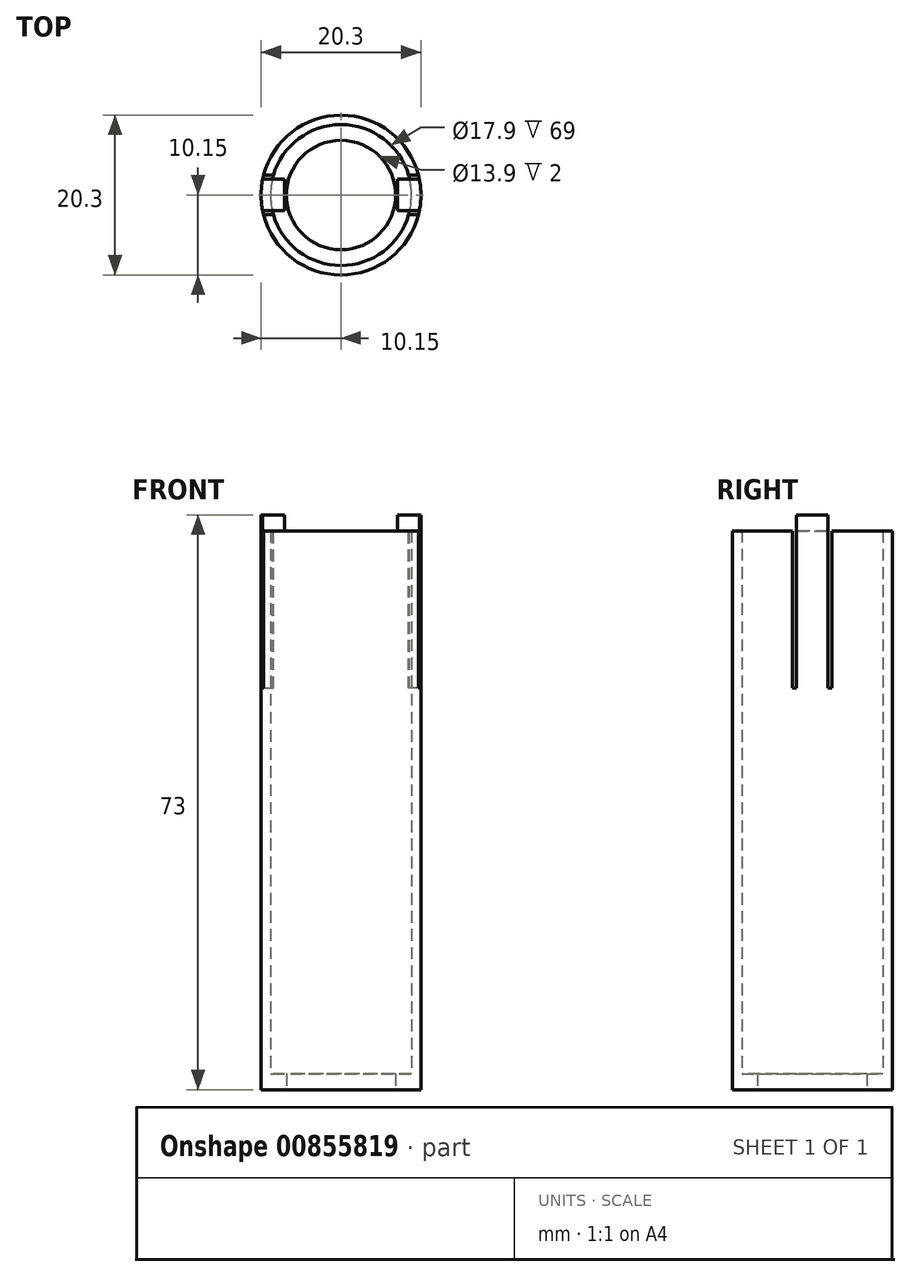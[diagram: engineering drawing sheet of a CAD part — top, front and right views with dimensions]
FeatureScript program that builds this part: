
annotation { "Feature Type Name" : "Feature", "Feature Type Description" : "" }
export const myFeature = defineFeature(function(context is Context, id is Id, definition is map)
    precondition{}
    {
        {
            var Q0;
            Q0=qCreatedBy(makeId("Top.planeOp"),FACE);
            var sketch = newSketch(context, id + "F0", { "sketchPlane" : qUnion([Q0])});
            skCircle(sketch, "E0", {"center": v(0, 0) * mm, "radius": 10.15 * mm});
            skCircle(sketch, "E1", {"center": v(0, 0) * mm, "radius": 8.95 * mm});
            skCircle(sketch, "E2", {"center": v(0, 0) * mm, "radius": 6.95 * mm});
            skSolve(sketch);
        }
        {
            var Q0;
            Q0 = qSketchRegion(id + "F0", true);
            extrude(context, id + "F1", {"entities" : qUnion([Q0]), "depth" : 71 * mm, "offsetDistance" : 25 * mm});
        }
        {
            var Q0;
            Q0=makeQuery(id+"F0.imprint","IMPRINT",FACE,{"disambiguationData":[TD([[makeQuery(id+"F0.imprint","IMPRINT",EDGE,{"derivedFrom":sQuery(id+"F0.wireOp",EDGE,"E1")}),1.0]])]});
            extrude(context, id + "F2", {"entities" : qUnion([Q0]), "operationType" : NewBodyOperationType.ADD, "depth" : 2 * mm, "offsetDistance" : 25 * mm});
        }
        {
            var Q0;
            Q0=makeQuery(id+"F1.opExtrude","CAP_FACE",FACE,{"disambiguationData":[OSD([sQuery(id+"F0.wireOp",EDGE,"E0"),sQuery(id+"F0.wireOp",EDGE,"E1")])],"isStart":false});
            var sketch = newSketch(context, id + "F3", { "sketchPlane" : qUnion([Q0])});
            skCircle(sketch, "E3.0", {"center": v(0, 0) * mm, "radius": 10.15 * mm});
            skCircle(sketch, "E4.0", {"center": v(0, 0) * mm, "radius": 8.95 * mm, "construction": true});
            skLineSegment(sketch, "E5", {"start": v(0, 0) * mm, "end": v(-8.95, 0) * mm, "construction": true});
            skLineSegment(sketch, "E6.bottom", {"start": v(-11.5, -2.5) * mm, "end": v(-6.4, -2.5) * mm});
            skLineSegment(sketch, "E6.top", {"start": v(-11.5, 2.5) * mm, "end": v(-6.4, 2.5) * mm});
            skLineSegment(sketch, "E6.left", {"start": v(-11.5, -2.5) * mm, "end": v(-11.5, 2.5) * mm});
            skLineSegment(sketch, "E6.right", {"start": v(-6.4, -2.5) * mm, "end": v(-6.4, 2.5) * mm});
            skPoint(sketch, "E6.middle", {"position": v(-8.95, 0) * mm});
            skLineSegment(sketch, "E7.bottom", {"start": v(-10.75, -2) * mm, "end": v(-7.15, -2) * mm});
            skLineSegment(sketch, "E7.top", {"start": v(-10.75, 2) * mm, "end": v(-7.15, 2) * mm});
            skLineSegment(sketch, "E7.left", {"start": v(-10.75, -2.2) * mm, "end": v(-10.75, 2) * mm});
            skLineSegment(sketch, "E7.right", {"start": v(-7.15, -2) * mm, "end": v(-7.15, 2) * mm});
            skLineSegment(sketch, "E8", {"start": v(0, 0) * mm, "end": v(0, 3.04) * mm, "construction": true});
            skPoint(sketch, "E9.MirrorP", {"position": v(8.95, 0) * mm});
            skLineSegment(sketch, "E10.MirrorCS", {"start": v(10.75, -2.2) * mm, "end": v(10.75, 2) * mm});
            skLineSegment(sketch, "E11.MirrorCS", {"start": v(6.4, -2.5) * mm, "end": v(6.4, 2.5) * mm});
            skLineSegment(sketch, "E12.MirrorCS", {"start": v(11.5, 2.5) * mm, "end": v(6.4, 2.5) * mm});
            skLineSegment(sketch, "E13.MirrorCS", {"start": v(10.75, -2) * mm, "end": v(7.15, -2) * mm});
            skLineSegment(sketch, "E14.MirrorCS", {"start": v(11.5, -2.5) * mm, "end": v(11.5, 2.5) * mm});
            skLineSegment(sketch, "E15.MirrorCS", {"start": v(7.15, -2) * mm, "end": v(7.15, 2) * mm});
            skLineSegment(sketch, "E16.MirrorCS", {"start": v(11.5, -2.5) * mm, "end": v(6.4, -2.5) * mm});
            skLineSegment(sketch, "E17.MirrorCS", {"start": v(10.75, 2) * mm, "end": v(7.15, 2) * mm});
            skSolve(sketch);
        }
        {
            var Q0;
            {var subQ0=sQuery(id+"F3.wireOp",EDGE,"E6.top");var subQ1=makeQuery(id+"F1.opExtrude","CAP_EDGE",EDGE,{"disambiguationData":[OSD([sQuery(id+"F0.wireOp",EDGE,"E0")])],"isStart":false});var subQ2=makeQuery(id+"F3.imprint","INTERSECT",VERTEX,{"derivedFrom":[subQ1,subQ0]});Q0=makeQuery(id+"F3.imprint","IMPRINT",FACE,{"disambiguationData":[TD([[makeQuery(id+"F3.imprint","IMPRINT",EDGE,{"disambiguationData":[TD([[subQ2,-1.0]])],"derivedFrom":subQ0}),-1.0]])]});}
            var Q1;
            {var subQ0=sQuery(id+"F3.wireOp",EDGE,"E6.bottom");var subQ1=makeQuery(id+"F1.opExtrude","CAP_EDGE",EDGE,{"disambiguationData":[OSD([sQuery(id+"F0.wireOp",EDGE,"E0")])],"isStart":false});var subQ2=makeQuery(id+"F3.imprint","INTERSECT",VERTEX,{"derivedFrom":[subQ1,subQ0]});Q1=makeQuery(id+"F3.imprint","IMPRINT",FACE,{"disambiguationData":[TD([[makeQuery(id+"F3.imprint","IMPRINT",EDGE,{"disambiguationData":[TD([[subQ2,-1.0]])],"derivedFrom":subQ0}),1.0]])]});}
            var Q2;
            {var subQ0=sQuery(id+"F3.wireOp",EDGE,"E12.MirrorCS");var subQ1=sQuery(id+"F3.wireOp",EDGE,"E3.0");var subQ2=makeQuery(id+"F3.imprint","INTERSECT",VERTEX,{"derivedFrom":[subQ1,subQ0]});Q2=makeQuery(id+"F3.imprint","IMPRINT",FACE,{"disambiguationData":[TD([[makeQuery(id+"F3.imprint","IMPRINT",EDGE,{"disambiguationData":[TD([[subQ2,1.0]])],"derivedFrom":subQ1}),1.0]])]});}
            var Q3;
            {var subQ0=sQuery(id+"F3.wireOp",EDGE,"E16.MirrorCS");var subQ1=sQuery(id+"F3.wireOp",EDGE,"E3.0");var subQ2=makeQuery(id+"F3.imprint","INTERSECT",VERTEX,{"derivedFrom":[subQ1,subQ0]});Q3=makeQuery(id+"F3.imprint","IMPRINT",FACE,{"disambiguationData":[TD([[makeQuery(id+"F3.imprint","IMPRINT",EDGE,{"disambiguationData":[TD([[subQ2,-1.0]])],"derivedFrom":subQ1}),1.0]])]});}
            extrude(context, id + "F4", {"entities" : qUnion([Q0, Q1, Q2, Q3]), "operationType" : NewBodyOperationType.REMOVE, "oppositeDirection" : true, "depth" : 20 * mm, "offsetDistance" : 25 * mm});
        }
        {
            var Q0;
            {var subQ0=sQuery(id+"F3.wireOp",EDGE,"E7.right");Q0=makeQuery(id+"F3.imprint","IMPRINT",FACE,{"disambiguationData":[TD([[makeQuery(id+"F3.imprint","IMPRINT",EDGE,{"derivedFrom":subQ0}),1.0]])]});}
            var Q1;
            {var subQ0=sQuery(id+"F3.wireOp",EDGE,"E7.top");var subQ1=sQuery(id+"F3.wireOp",EDGE,"E3.0");var subQ2=makeQuery(id+"F3.imprint","INTERSECT",VERTEX,{"derivedFrom":[subQ1,subQ0]});Q1=makeQuery(id+"F3.imprint","IMPRINT",FACE,{"disambiguationData":[TD([[makeQuery(id+"F3.imprint","IMPRINT",EDGE,{"disambiguationData":[TD([[subQ2,-1.0]])],"derivedFrom":subQ1}),1.0]])]});}
            var Q2;
            {var subQ0=sQuery(id+"F3.wireOp",EDGE,"E15.MirrorCS");Q2=makeQuery(id+"F3.imprint","IMPRINT",FACE,{"disambiguationData":[TD([[makeQuery(id+"F3.imprint","IMPRINT",EDGE,{"derivedFrom":subQ0}),-1.0]])]});}
            var Q3;
            {var subQ0=sQuery(id+"F3.wireOp",EDGE,"E17.MirrorCS");var subQ1=sQuery(id+"F3.wireOp",EDGE,"E3.0");var subQ2=makeQuery(id+"F3.imprint","INTERSECT",VERTEX,{"derivedFrom":[subQ1,subQ0]});Q3=makeQuery(id+"F3.imprint","IMPRINT",FACE,{"disambiguationData":[TD([[makeQuery(id+"F3.imprint","IMPRINT",EDGE,{"disambiguationData":[TD([[subQ2,1.0]])],"derivedFrom":subQ1}),1.0]])]});}
            extrude(context, id + "F5", {"entities" : qUnion([Q0, Q1, Q2, Q3]), "operationType" : NewBodyOperationType.ADD, "depth" : 2 * mm, "offsetDistance" : 25 * mm});
        }
    });
